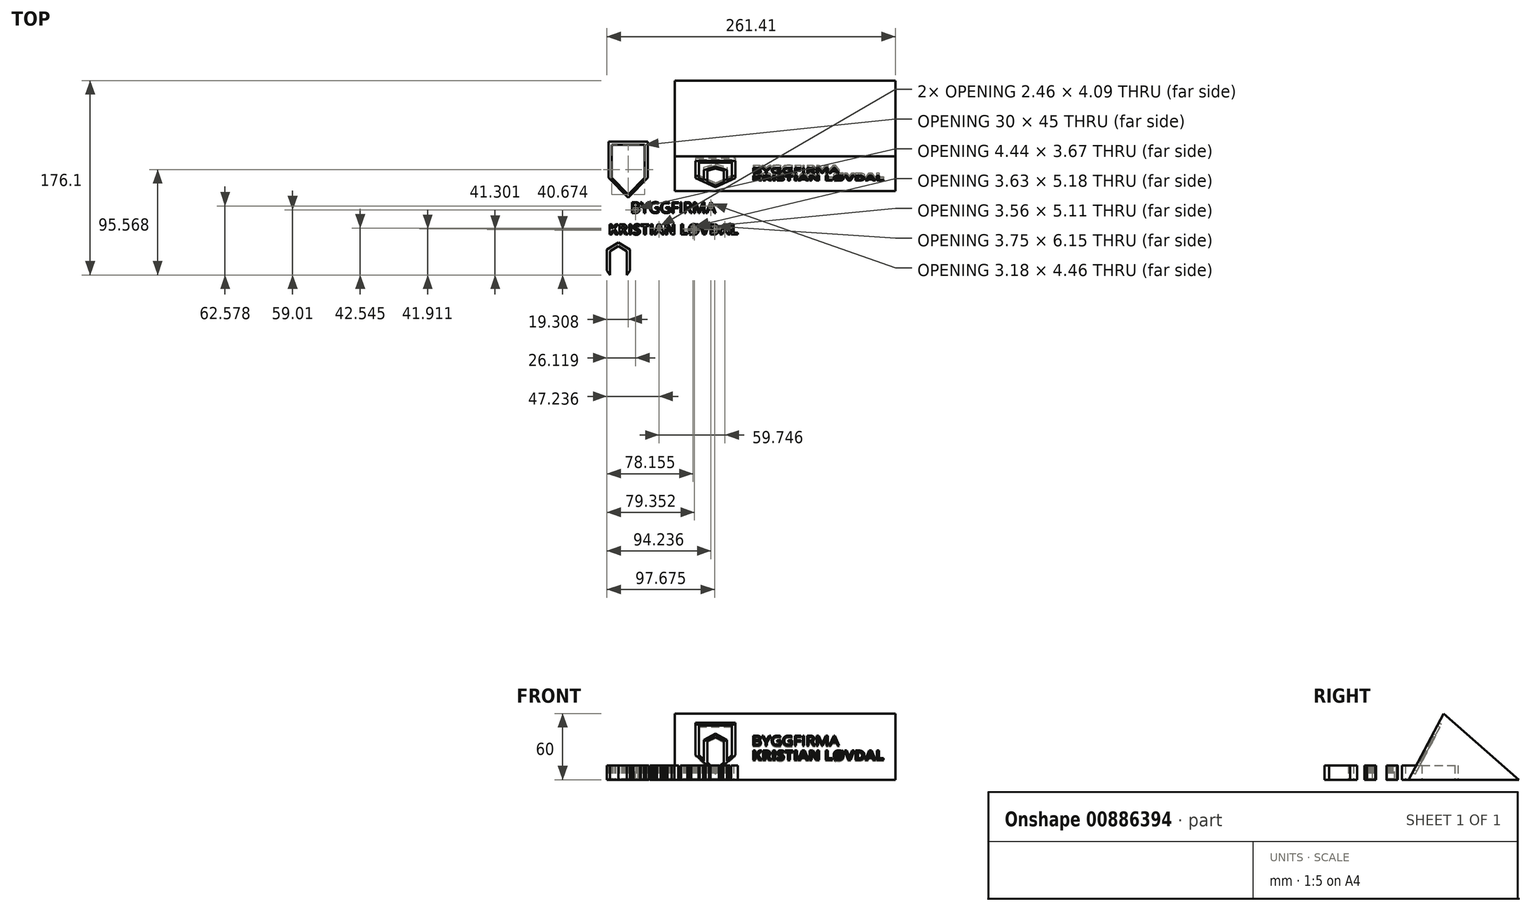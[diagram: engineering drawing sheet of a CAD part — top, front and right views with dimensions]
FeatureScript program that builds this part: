
annotation { "Feature Type Name" : "Feature", "Feature Type Description" : "" }
export const myFeature = defineFeature(function(context is Context, id is Id, definition is map)
    precondition{}
    {
        {
            var Q0;
            Q0=qCreatedBy(makeId("Top.planeOp"),FACE);
            var sketch = newSketch(context, id + "F0", { "sketchPlane" : qUnion([Q0])});
            skLineSegment(sketch, "E0.bottom", {"start": v(-100, 100) * mm, "end": v(100, 100) * mm});
            skLineSegment(sketch, "E0.top", {"start": v(-100, 0) * mm, "end": v(100, 0) * mm});
            skLineSegment(sketch, "E0.left", {"start": v(-100, 100) * mm, "end": v(-100, 0) * mm});
            skLineSegment(sketch, "E0.right", {"start": v(100, 100) * mm, "end": v(100, 0) * mm});
            skSolve(sketch);
        }
        {
            var Q0;
            Q0=qCreatedBy(makeId("Right.planeOp"),FACE);
            var sketch = newSketch(context, id + "F1", { "sketchPlane" : qUnion([Q0])});
            skLineSegment(sketch, "E1", {"start": v(100, 0) * mm, "end": v(31.57, 60) * mm});
            skLineSegment(sketch, "E2", {"start": v(31.57, 60) * mm, "end": v(0, 0) * mm});
            skLineSegment(sketch, "E3", {"start": v(100, 0) * mm, "end": v(0, 0) * mm});
            skSolve(sketch);
        }
        {
            var Q0;
            Q0=makeQuery(id+"F1.imprint","IMPRINT",FACE,{"disambiguationData":[TD([[makeQuery(id+"F1.imprint","IMPRINT",EDGE,{"derivedFrom":sQuery(id+"F1.wireOp",EDGE,"E1")}),1.0]])]});
            extrude(context, id + "F2", {"entities" : qUnion([Q0]), "depth" : 200 * mm, "offsetDistance" : 25 * mm});
        }
        {
            var Q0;
            Q0=makeQuery(id+"F2.opExtrude","SWEPT_FACE",FACE,{"disambiguationData":[OSD([sQuery(id+"F1.wireOp",EDGE,"E2")])]});
            var sketch = newSketch(context, id + "F3", { "sketchPlane" : qUnion([Q0])});
            skText(sketch, "E4", { "text": "BYGGFIRMA", "fontName": "OpenSans-Regular.ttf"});
            const initialGuessF3  = {"E4": [0.07, 0.035, 1, 0, 0.01015]};
            skSetInitialGuess(sketch, initialGuessF3);
            skSolve(sketch);
        }
        {
            var Q0;
            Q0=makeQuery(id+"F3.imprint","IMPRINT",FACE,{"disambiguationData":[TD([[makeQuery(id+"F3.imprint","IMPRINT",EDGE,{"derivedFrom":sQuery(id+"F3.wireOp",EDGE,"E4.sketch_text.stroke-0")}),1.0]])]});
            var sketch = newSketch(context, id + "F4", { "sketchPlane" : qUnion([Q0])});
            skText(sketch, "E5", { "text": "KRISTIAN LØVDAL", "fontName": "OpenSans-Bold.ttf"});
            const initialGuessF4  = {"E5": [0.07, 0.0203, 1, 0, 0.0097]};
            skSetInitialGuess(sketch, initialGuessF4);
            skSolve(sketch);
        }
        {
            var Q0;
            Q0=qSketchRegion(id+"F4",true);
            extrude(context, id + "F5", {"entities" : qUnion([Q0]), "operationType" : NewBodyOperationType.REMOVE, "oppositeDirection" : true, "depth" : 3 * mm, "offsetDistance" : 25 * mm});
        }
        {
            var Q0;
            Q0=qSketchRegion(id+"F3",true);
            extrude(context, id + "F6", {"entities" : qUnion([Q0]), "operationType" : NewBodyOperationType.REMOVE, "oppositeDirection" : true, "depth" : 3 * mm, "offsetDistance" : 25 * mm});
        }
        {
            var Q0;
            Q0=qCreatedBy(makeId("Top.planeOp"),FACE);
            var sketch = newSketch(context, id + "F7", { "sketchPlane" : qUnion([Q0])});
            skText(sketch, "E6", { "text": "BYGGFIRMA", "fontName": "OpenSans-Regular.ttf"});
            const initialGuessF7  = {"E6": [-0.04, -0.0199, 1, 0, 0.0099]};
            skSetInitialGuess(sketch, initialGuessF7);
            skSolve(sketch);
        }
        {
            var Q0;
            Q0=qCreatedBy(makeId("Top.planeOp"),FACE);
            var sketch = newSketch(context, id + "F8", { "sketchPlane" : qUnion([Q0])});
            skText(sketch, "E7", { "text": "KRISTIAN LØVDAL", "fontName": "OpenSans-Bold.ttf"});
            const initialGuessF8  = {"E7": [-0.06, -0.03953, 1, 0, 0.00953]};
            skSetInitialGuess(sketch, initialGuessF8);
            skSolve(sketch);
        }
        {
            var Q0;
            Q0=qSketchRegion(id+"F7",true);
            extrude(context, id + "F9", {"entities" : qUnion([Q0]), "operationType" : NewBodyOperationType.ADD, "depth" : 13 * mm, "offsetDistance" : 25 * mm});
        }
        {
            var Q0;
            Q0=qSketchRegion(id+"F8",true);
            extrude(context, id + "F10", {"entities" : qUnion([Q0]), "operationType" : NewBodyOperationType.ADD, "depth" : 13 * mm, "offsetDistance" : 25 * mm});
        }
        {
            var Q0;
            {var subQ76=sQuery(id+"F1.wireOp",EDGE,"E1");var subQ77=makeQuery(id+"F2.opExtrude","SWEPT_FACE",FACE,{"disambiguationData":[OSD([subQ76])]});var subQ82=sQuery(id+"F1.wireOp",EDGE,"E2");Q0=makeQuery(id+"F6.boolean.opBoolean","SPLIT",FACE,{"disambiguationData":[TD([subQ77])],"derivedFrom":makeQuery(id+"F5.boolean.opBoolean","SPLIT",FACE,{"disambiguationData":[TD([subQ77])],"derivedFrom":makeQuery(id+"F2.opExtrude","SWEPT_FACE",FACE,{"disambiguationData":[OSD([subQ82])]})})});}
            var sketch = newSketch(context, id + "F11", { "sketchPlane" : qUnion([Q0])});
            skLineSegment(sketch, "E8", {"start": v(52, 55.3) * mm, "end": v(22, 55.3) * mm});
            skLineSegment(sketch, "E9", {"start": v(22, 55.3) * mm, "end": v(22, 25.3) * mm});
            skLineSegment(sketch, "E10", {"start": v(22, 25.3) * mm, "end": v(37, 10.3) * mm});
            skLineSegment(sketch, "E11", {"start": v(37, 10.3) * mm, "end": v(52, 25.3) * mm});
            skLineSegment(sketch, "E12", {"start": v(52, 25.3) * mm, "end": v(52, 55.3) * mm});
            skSolve(sketch);
        }
        {
            var Q0;
            Q0=makeQuery(id+"F11.imprint","IMPRINT",FACE,{"disambiguationData":[TD([[makeQuery(id+"F11.imprint","IMPRINT",EDGE,{"derivedFrom":sQuery(id+"F11.wireOp",EDGE,"E8")}),1.0]])]});
            var sketch = newSketch(context, id + "F12", { "sketchPlane" : qUnion([Q0])});
            skLineSegment(sketch, "E13", {"start": v(19, 58.3) * mm, "end": v(55, 58.3) * mm});
            skLineSegment(sketch, "E14", {"start": v(55, 58.3) * mm, "end": v(55, 25.3) * mm});
            skLineSegment(sketch, "E15", {"start": v(55, 25.3) * mm, "end": v(37, 7.3) * mm});
            skLineSegment(sketch, "E16", {"start": v(37, 7.3) * mm, "end": v(19, 25.3) * mm});
            skLineSegment(sketch, "E17", {"start": v(19, 25.3) * mm, "end": v(19, 58.3) * mm});
            skSolve(sketch);
        }
        {
            var Q0;
            Q0=makeQuery(id+"F12.imprint","IMPRINT",FACE,{"disambiguationData":[TD([[makeQuery(id+"F12.imprint","IMPRINT",EDGE,{"derivedFrom":sQuery(id+"F12.wireOp",EDGE,"E13")}),-1.0]])]});
            extrude(context, id + "F13", {"entities" : qUnion([Q0]), "operationType" : NewBodyOperationType.REMOVE, "oppositeDirection" : true, "depth" : 3 * mm, "offsetDistance" : 25 * mm});
        }
        {
            var Q0;
            Q0=qCreatedBy(makeId("Top.planeOp"),FACE);
            var sketch = newSketch(context, id + "F14", { "sketchPlane" : qUnion([Q0])});
            skLineSegment(sketch, "E18", {"start": v(-57.1, 41.97) * mm, "end": v(-27.1, 41.97) * mm});
            skLineSegment(sketch, "E19", {"start": v(-27.1, 41.97) * mm, "end": v(-27.1, 11.97) * mm});
            skLineSegment(sketch, "E20", {"start": v(-27.1, 11.97) * mm, "end": v(-42.1, -3.03) * mm});
            skLineSegment(sketch, "E21", {"start": v(-42.1, -3.03) * mm, "end": v(-57.1, 11.97) * mm});
            skLineSegment(sketch, "E22", {"start": v(-57.1, 11.97) * mm, "end": v(-57.1, 41.97) * mm});
            skSolve(sketch);
        }
        {
            var Q0;
            Q0=qCreatedBy(makeId("Top.planeOp"),FACE);
            var sketch = newSketch(context, id + "F15", { "sketchPlane" : qUnion([Q0])});
            skLineSegment(sketch, "E23", {"start": v(-60, 44.87) * mm, "end": v(-24.2, 44.87) * mm});
            skLineSegment(sketch, "E24", {"start": v(-24.2, 44.87) * mm, "end": v(-24.2, 11.97) * mm});
            skLineSegment(sketch, "E25", {"start": v(-24.2, 11.97) * mm, "end": v(-42.1, -5.93) * mm});
            skLineSegment(sketch, "E26", {"start": v(-42.1, -5.93) * mm, "end": v(-60, 11.97) * mm});
            skLineSegment(sketch, "E27", {"start": v(-60, 11.97) * mm, "end": v(-60, 44.87) * mm});
            skSolve(sketch);
        }
        {
            var Q0;
            Q0=qSketchRegion(id+"F15",true);
            extrude(context, id + "F16", {"entities" : qUnion([Q0]), "operationType" : NewBodyOperationType.ADD, "depth" : 13 * mm, "offsetDistance" : 25 * mm});
        }
        {
            var Q0;
            Q0=qSketchRegion(id+"F14",true);
            extrude(context, id + "F17", {"entities" : qUnion([Q0]), "operationType" : NewBodyOperationType.REMOVE, "depth" : 25 * mm, "offsetDistance" : 25 * mm});
        }
        {
            var Q0;
            Q0=makeQuery(id+"F11.imprint","IMPRINT",FACE,{"disambiguationData":[TD([[makeQuery(id+"F11.imprint","IMPRINT",EDGE,{"derivedFrom":sQuery(id+"F11.wireOp",EDGE,"E8")}),1.0]])]});
            var sketch = newSketch(context, id + "F18", { "sketchPlane" : qUnion([Q0])});
            skLineSegment(sketch, "E28", {"start": v(26.5, 20.8) * mm, "end": v(26.5, 40.8) * mm});
            skLineSegment(sketch, "E29", {"start": v(26.5, 40.8) * mm, "end": v(37, 47.3) * mm});
            skLineSegment(sketch, "E30", {"start": v(37, 47.3) * mm, "end": v(47.5, 40.8) * mm});
            skLineSegment(sketch, "E31", {"start": v(47.5, 40.8) * mm, "end": v(47.5, 20.8) * mm});
            skLineSegment(sketch, "E32", {"start": v(47.5, 20.8) * mm, "end": v(44.5, 17.8) * mm});
            skLineSegment(sketch, "E33", {"start": v(44.5, 17.8) * mm, "end": v(44.5, 39.56) * mm});
            skLineSegment(sketch, "E34", {"start": v(44.5, 39.56) * mm, "end": v(37, 43.8) * mm});
            skLineSegment(sketch, "E35", {"start": v(37, 43.8) * mm, "end": v(29.5, 39.56) * mm});
            skLineSegment(sketch, "E36", {"start": v(29.5, 39.56) * mm, "end": v(29.5, 17.8) * mm});
            skLineSegment(sketch, "E37", {"start": v(29.5, 17.8) * mm, "end": v(26.5, 20.8) * mm});
            skSolve(sketch);
        }
        {
            var Q0;
            {var subQ4=sQuery(id+"F18.wireOp",EDGE,"E29");Q0=makeQuery(id+"F18.imprint","IMPRINT",FACE,{"disambiguationData":[TD([[makeQuery(id+"F18.imprint","IMPRINT",EDGE,{"derivedFrom":subQ4}),-1.0]])]});}
            extrude(context, id + "F19", {"entities" : qUnion([Q0]), "operationType" : NewBodyOperationType.REMOVE, "oppositeDirection" : true, "depth" : 3 * mm, "offsetDistance" : 25 * mm});
        }
        {
            var Q0;
            Q0=qCreatedBy(makeId("Top.planeOp"),FACE);
            var sketch = newSketch(context, id + "F20", { "sketchPlane" : qUnion([Q0])});
            skLineSegment(sketch, "E38", {"start": v(-61.41, -71.95) * mm, "end": v(-61.41, -52.95) * mm});
            skLineSegment(sketch, "E39", {"start": v(-61.41, -52.95) * mm, "end": v(-51.01, -46.6) * mm});
            skLineSegment(sketch, "E40", {"start": v(-51.01, -46.6) * mm, "end": v(-40.61, -52.95) * mm});
            skLineSegment(sketch, "E41", {"start": v(-40.61, -52.95) * mm, "end": v(-40.61, -71.95) * mm});
            skLineSegment(sketch, "E42", {"start": v(-40.61, -71.95) * mm, "end": v(-43.41, -76.1) * mm});
            skLineSegment(sketch, "E43", {"start": v(-43.41, -76.1) * mm, "end": v(-43.41, -54.54) * mm});
            skLineSegment(sketch, "E44", {"start": v(-43.41, -54.54) * mm, "end": v(-51.01, -49.9) * mm});
            skLineSegment(sketch, "E45", {"start": v(-51.01, -49.9) * mm, "end": v(-58.61, -54.54) * mm});
            skLineSegment(sketch, "E46", {"start": v(-58.61, -54.54) * mm, "end": v(-58.61, -76.1) * mm});
            skLineSegment(sketch, "E47", {"start": v(-58.61, -76.1) * mm, "end": v(-61.41, -71.95) * mm});
            skSolve(sketch);
        }
        {
            var Q0;
            Q0=qSketchRegion(id+"F20",true);
            extrude(context, id + "F21", {"entities" : qUnion([Q0]), "operationType" : NewBodyOperationType.ADD, "depth" : 13 * mm, "offsetDistance" : 25 * mm});
        }
    });
